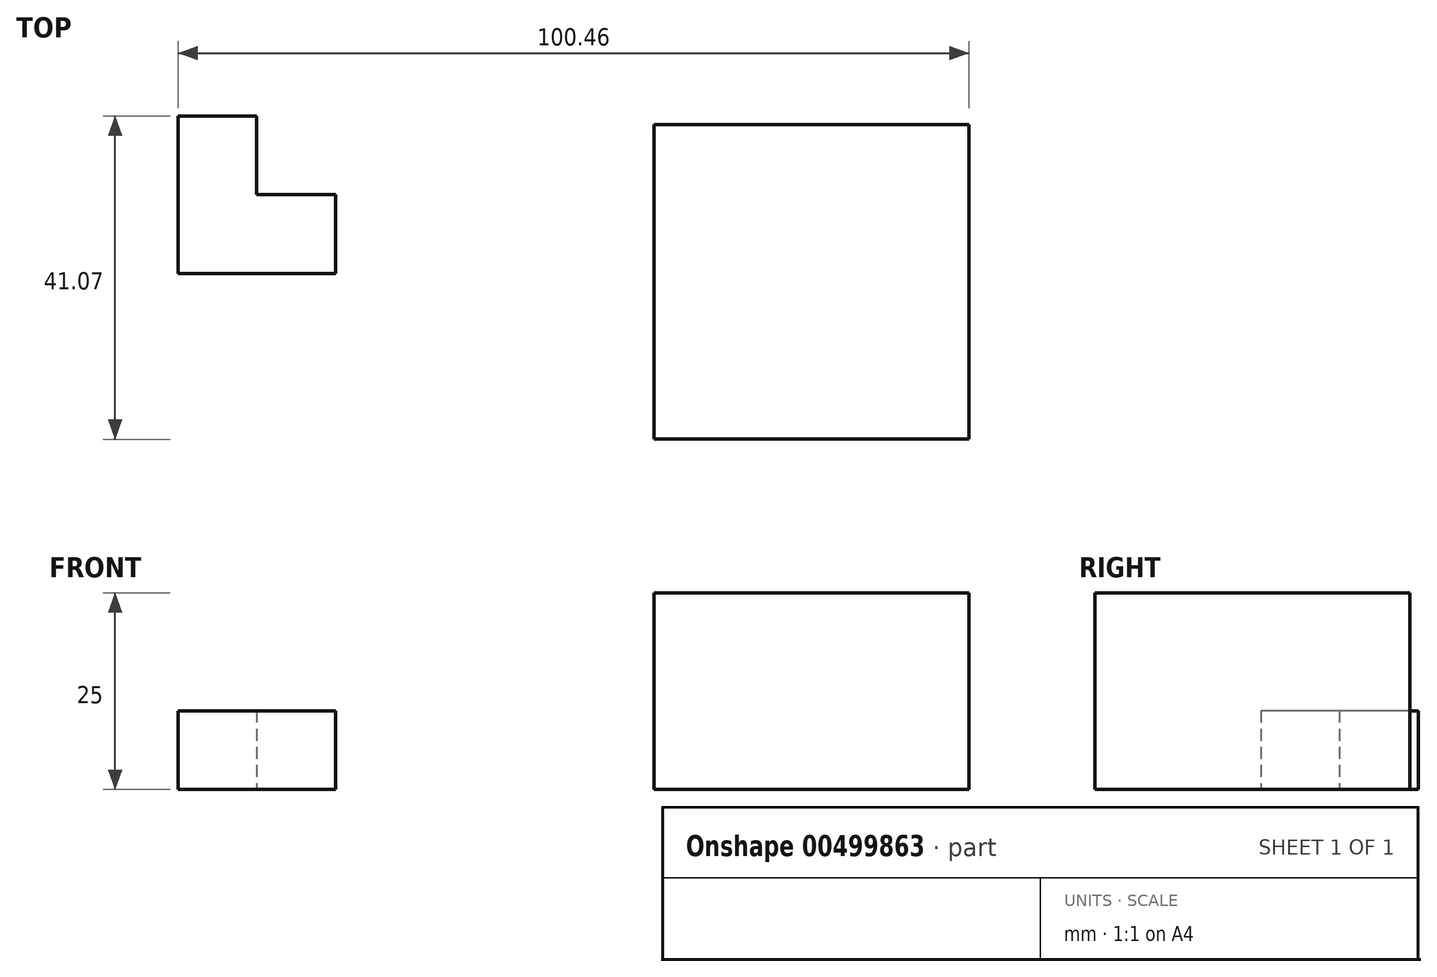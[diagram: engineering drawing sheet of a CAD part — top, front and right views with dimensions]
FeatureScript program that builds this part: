
annotation { "Feature Type Name" : "Feature", "Feature Type Description" : "" }
export const myFeature = defineFeature(function(context is Context, id is Id, definition is map)
    precondition{}
    {
        {
            var Q0;
            Q0=qCreatedBy(makeId("Top.planeOp"),FACE);
            var sketch = newSketch(context, id + "F0", { "sketchPlane" : qUnion([Q0])});
            skLineSegment(sketch, "E0.bottom", {"start": v(-36, 7.46) * mm, "end": v(-26, 7.46) * mm});
            skLineSegment(sketch, "E0.top", {"start": v(-36, -12.54) * mm, "end": v(-16, -12.54) * mm});
            skLineSegment(sketch, "E0.left", {"start": v(-36, 7.46) * mm, "end": v(-36, -12.54) * mm});
            skLineSegment(sketch, "E0.right", {"start": v(-16, -2.54) * mm, "end": v(-16, -12.54) * mm});
            skLineSegment(sketch, "E1.top", {"start": v(-16, -2.54) * mm, "end": v(-26, -2.54) * mm});
            skLineSegment(sketch, "E1.right", {"start": v(-26, 7.46) * mm, "end": v(-26, -2.54) * mm});
            skSolve(sketch);
        }
        {
            var Q0;
            Q0=makeQuery(id+"F0.imprint","IMPRINT",FACE,{"disambiguationData":[TD([[makeQuery(id+"F0.imprint","IMPRINT",EDGE,{"derivedFrom":sQuery(id+"F0.wireOp",EDGE,"E0.bottom")}),-1.0]])]});
            extrude(context, id + "F1", {"entities" : qUnion([Q0]), "depth" : 10 * mm});
        }
        {
            var Q0;
            Q0=qCreatedBy(makeId("Top.planeOp"),FACE);
            var sketch = newSketch(context, id + "F2", { "sketchPlane" : qUnion([Q0])});
            skLineSegment(sketch, "E2.bottom", {"start": v(24.45, 6.4) * mm, "end": v(64.45, 6.4) * mm});
            skLineSegment(sketch, "E2.top", {"start": v(24.45, -33.6) * mm, "end": v(64.45, -33.6) * mm});
            skLineSegment(sketch, "E2.left", {"start": v(24.45, 6.4) * mm, "end": v(24.45, -33.6) * mm});
            skLineSegment(sketch, "E2.right", {"start": v(64.45, 6.4) * mm, "end": v(64.45, -33.6) * mm});
            skSolve(sketch);
        }
        {
            var Q0;
            Q0=makeQuery(id+"F2.imprint","IMPRINT",FACE,{"disambiguationData":[TD([[makeQuery(id+"F2.imprint","IMPRINT",EDGE,{"derivedFrom":sQuery(id+"F2.wireOp",EDGE,"E2.bottom")}),-1.0]])]});
            extrude(context, id + "F3", {"entities" : qUnion([Q0]), "depth" : 25 * mm});
        }
    });
